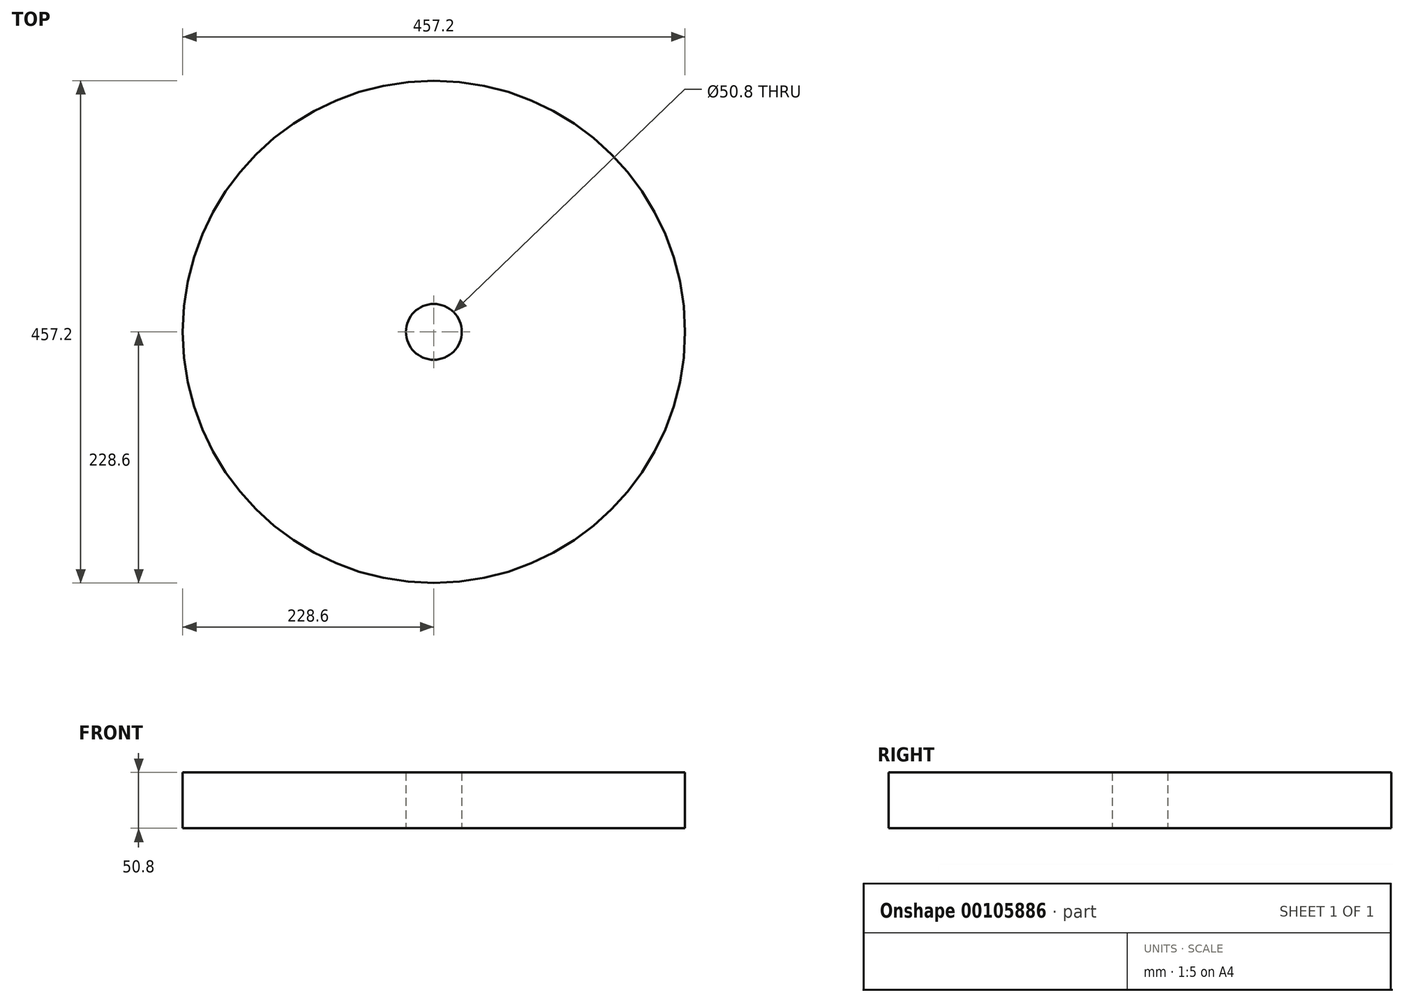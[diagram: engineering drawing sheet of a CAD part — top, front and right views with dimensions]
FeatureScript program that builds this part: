
annotation { "Feature Type Name" : "Feature", "Feature Type Description" : "" }
export const myFeature = defineFeature(function(context is Context, id is Id, definition is map)
    precondition{}
    {
        {
            var Q0;
            Q0=qCreatedBy(makeId("Top.planeOp"),FACE);
            var sketch = newSketch(context, id + "F0", { "sketchPlane" : qUnion([Q0])});
            skCircle(sketch, "E0", {"center": v(0, 0) * mm, "radius": 228.6 * mm});
            skCircle(sketch, "E1", {"center": v(0, 0) * mm, "radius": 25.4 * mm});
            skSolve(sketch);
        }
        {
            var Q0;
            Q0 = qSketchRegion(id + "F0", true);
            extrude(context, id + "F1", {"entities" : qUnion([Q0]), "depth" : 50.8 * mm});
        }
    });
